# Revit family: xxxShowerhead-American_Standard-Spectra_eTouch-9035474_Series
name_source: partatom
category: Plumbing Fixtures
units: mm (PartAtom-declared; Revit-internal decimal feet)

## family parameters
Cut with Voids When Loaded = No
Host = Face
OmniClass Number = 23.45.05.14.17
OmniClass Title = Showers
Part Type = Normal
Room Calculation Point = No
Round Connector Dimension = Use Diameter
Shared = Yes

## types (4) — shared parameters
1660.240 Shower Arm = Yes
1660.241 Shower Arm = No
ASME A112.18.1/CSA B125.1 = Yes
Assembly Code = D2020300
CW Connection = Yes
CWFU = 3
Cold Water Connection Diameter = 1/2"
Default Elevation = 0"
Description = Spectra® eTouch 7-Inch 2.5 gpm/9.5 L/min Fixed Showerhead
Flow Rate = 2.5 gpm/9.5 L/min
HW Connection = Yes
HWFU = 3
Hot Water Connection Diameter = 1/2"
Installation Instruction Link = https://americanstandard.box.com
Installation Type = Wall Mounted
Manufacturer = American Standard
Price = Prices may vary. Please consult Manufacturer Representative for most up-to-date price list.
Product Documentation Link = https://americanstandard.box.com
Product Page URL = https://www.americanstandard-us.com
Revised Date = 03/18/2022
Showerhead Diameter = 7 3/16"
Showerhead Height = 3 3/4"
Showerhead Mounting Height = 78"
Spectra eTouch Mounting Height = 44"
Tempered Water Connection = Yes
Tempered Water Connection Diameter = 1/2"
URL = https://www.americanstandard-us.com
Vent Connection = No
WFU = 4
Waste Connection = No
eTouch Constraint = 44"

## per-type parameters (varying)
| type | Finish | Material | Showerhead |
| 9035474.002 | Metal-American Standard-002-Polished Chrome | Metal-American Standard-002-Polished Chrome | Showerhead-American_Standard-Spectra_Rain-9038.374_Series : 9038374.002 |
| 9035474.013 | Metal-American Standard-013-Polished Nickel PVD | Metal-American Standard-013-Polished Nickel PVD | Showerhead-American_Standard-Spectra_Rain-9038.374_Series : 9038374.013 |
| 9035474.278 | Metal-American Standard-278-Legacy Bronze | Metal-American Standard-278-Legacy Bronze | Showerhead-American_Standard-Spectra_Rain-9038.374_Series : 9038374.278 |
| 9035474.295 | Metal-American Standard-295-Brushed Nickel | Metal-American Standard-295-Brushed Nickel | Showerhead-American_Standard-Spectra_Rain-9038.374_Series : 9038374.295 |

note: column(s) folded — value = type name in every type: Model

## geometry (parser evidence)
native form markers: Sweep x3
no freeform markers — native parametric forms only
